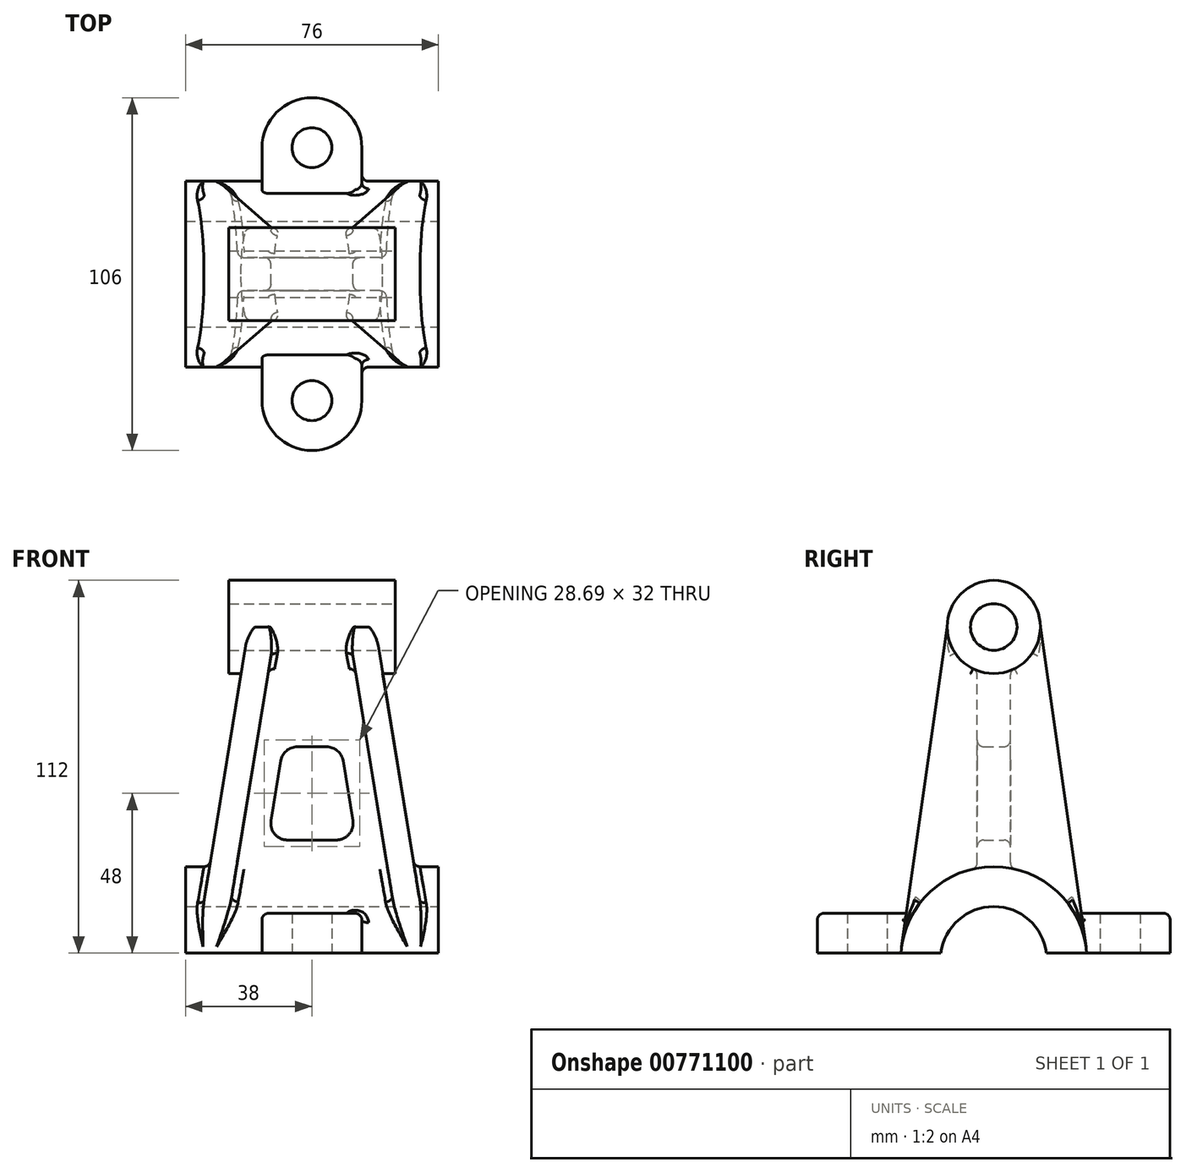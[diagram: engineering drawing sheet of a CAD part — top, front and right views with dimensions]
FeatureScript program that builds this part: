
annotation { "Feature Type Name" : "Feature", "Feature Type Description" : "" }
export const myFeature = defineFeature(function(context is Context, id is Id, definition is map)
    precondition{}
    {
        {
            var Q0;
            Q0=qCreatedBy(makeId("Right.planeOp"),FACE);
            var sketch = newSketch(context, id + "F0", { "sketchPlane" : qUnion([Q0])});
            skArc(sketch, "E0", {"start": v(27.93, 2) * mm, "mid": v(0, 28) * mm, "end": v(-27.93, 2) * mm});
            skArc(sketch, "E1", {"start": v(15.87, 2) * mm, "mid": v(0, 16) * mm, "end": v(-15.87, 2) * mm});
            skLineSegment(sketch, "E2", {"start": v(0, 0) * mm, "end": v(36.01, 0) * mm, "construction": true});
            skLineSegment(sketch, "E3", {"start": v(-27.93, 2) * mm, "end": v(27.93, 2) * mm});
            skSolve(sketch);
        }
        {
            var Q0;
            Q0=qSketchRegion(id+"F0",true);
            extrude(context, id + "F1", {"entities" : qUnion([Q0]), "depth" : 76 * mm, "offsetDistance" : 25 * mm, "symmetric" : true});
        }
        {
            var Q0;
            Q0=qCreatedBy(makeId("Right.planeOp"),FACE);
            var sketch = newSketch(context, id + "F2", { "sketchPlane" : qUnion([Q0])});
            skLineSegment(sketch, "E4", {"start": v(0, 0) * mm, "end": v(0, 100) * mm, "construction": true});
            skCircle(sketch, "E5", {"center": v(0, 100) * mm, "radius": 7 * mm});
            skCircle(sketch, "E6", {"center": v(0, 100) * mm, "radius": 14 * mm});
            skSolve(sketch);
        }
        {
            var Q0;
            Q0=qSketchRegion(id+"F2",true);
            var Q1;
            Q1=makeQuery(id+"F2.imprint","IMPRINT",FACE,{"disambiguationData":[TD([[makeQuery(id+"F2.imprint","IMPRINT",EDGE,{"derivedFrom":sQuery(id+"F2.wireOp",EDGE,"E5")}),1.0]])]});
            extrude(context, id + "F3", {"entities" : qUnion([Q0, Q1]), "depth" : 50 * mm, "offsetDistance" : 25 * mm, "symmetric" : true});
        }
        {
            var Q0;
            Q0=qCreatedBy(makeId("Front.planeOp"),FACE);
            var sketch = newSketch(context, id + "F4", { "sketchPlane" : qUnion([Q0])});
            skLineSegment(sketch, "E7", {"start": v(0, 0) * mm, "end": v(0, 29.66) * mm, "construction": true});
            skLineSegment(sketch, "E8", {"start": v(-19, 100) * mm, "end": v(19, 100) * mm});
            skLineSegment(sketch, "E9.0", {"start": v(35, 2) * mm, "end": v(-35, 2) * mm});
            skLineSegment(sketch, "E10", {"start": v(19, 100) * mm, "end": v(35, 2) * mm});
            skLineSegment(sketch, "E11.MirrorCS", {"start": v(-19, 100) * mm, "end": v(-35, 2) * mm});
            skLineSegment(sketch, "E12", {"start": v(-30.76, 28) * mm, "end": v(30.76, 28) * mm});
            skLineSegment(sketch, "E13.0", {"start": v(9.35, 59.8) * mm, "end": v(12.29, 41.8) * mm});
            skLineSegment(sketch, "E14.MirrorCS", {"start": v(-9.35, 59.8) * mm, "end": v(-12.29, 41.8) * mm});
            skLineSegment(sketch, "E15.trimOffspring", {"start": v(-4.42, 64) * mm, "end": v(4.42, 64) * mm});
            skLineSegment(sketch, "E16.trimOffspring", {"start": v(-7.35, 36) * mm, "end": v(7.35, 36) * mm});
            skPoint(sketch, "E17.orphan", {"position": v(-38, 2) * mm});
            skPoint(sketch, "E18.orphan", {"position": v(38, 2) * mm});
            skLineSegment(sketch, "E19", {"start": v(10.9, 100) * mm, "end": v(26.9, 2) * mm});
            skLineSegment(sketch, "E20.MirrorCS", {"start": v(-10.9, 100) * mm, "end": v(-26.9, 2) * mm});
            skPoint(sketch, "E21.visualSharp", {"position": v(-8.67, 64) * mm});
            skArc(sketch, "E21.filletArc", {"start": v(-4.42, 64) * mm, "mid": v(-7.65, 62.8) * mm, "end": v(-9.35, 59.8) * mm});
            skPoint(sketch, "E22.visualSharp", {"position": v(8.67, 64) * mm});
            skArc(sketch, "E22.filletArc", {"start": v(9.35, 59.8) * mm, "mid": v(7.65, 62.8) * mm, "end": v(4.42, 64) * mm});
            skPoint(sketch, "E23.visualSharp", {"position": v(-13.24, 36) * mm});
            skArc(sketch, "E23.filletArc", {"start": v(-12.29, 41.8) * mm, "mid": v(-11.16, 37.76) * mm, "end": v(-7.35, 36) * mm});
            skPoint(sketch, "E24.visualSharp", {"position": v(13.24, 36) * mm});
            skArc(sketch, "E24.filletArc", {"start": v(7.35, 36) * mm, "mid": v(11.16, 37.76) * mm, "end": v(12.29, 41.8) * mm});
            skSolve(sketch);
        }
        {
            var Q0;
            Q0=qSketchRegion(id+"F4",true);
            extrude(context, id + "F5", {"entities" : qUnion([Q0]), "operationType" : NewBodyOperationType.ADD, "depth" : 10 * mm, "offsetDistance" : 25 * mm, "symmetric" : true});
        }
        {
            var Q0;
            {var subQ0=sQuery(id+"F4.wireOp",EDGE,"E10");var subQ1=sQuery(id+"F4.wireOp",EDGE,"E8");var subQ2=makeQuery(id+"F4.imprint","INTERSECT",VERTEX,{"derivedFrom":[subQ1,subQ0]});Q0=makeQuery(id+"F4.imprint","IMPRINT",FACE,{"disambiguationData":[TD([[makeQuery(id+"F4.imprint","IMPRINT",EDGE,{"disambiguationData":[TD([[subQ2,1.0]])],"derivedFrom":subQ1}),-1.0]])]});}
            var Q1;
            {var subQ0=sQuery(id+"F4.wireOp",EDGE,"E11.MirrorCS");var subQ1=sQuery(id+"F4.wireOp",EDGE,"E8");var subQ2=makeQuery(id+"F4.imprint","INTERSECT",VERTEX,{"derivedFrom":[subQ1,subQ0]});Q1=makeQuery(id+"F4.imprint","IMPRINT",FACE,{"disambiguationData":[TD([[makeQuery(id+"F4.imprint","IMPRINT",EDGE,{"disambiguationData":[TD([[subQ2,-1.0]])],"derivedFrom":subQ1}),-1.0]])]});}
            var Q2;
            {var subQ0=sQuery(id+"F4.wireOp",EDGE,"E11.MirrorCS");var subQ1=sQuery(id+"F4.wireOp",EDGE,"E9.0");var subQ2=makeQuery(id+"F4.imprint","INTERSECT",VERTEX,{"derivedFrom":[subQ1,subQ0]});Q2=makeQuery(id+"F4.imprint","IMPRINT",FACE,{"disambiguationData":[TD([[makeQuery(id+"F4.imprint","IMPRINT",EDGE,{"disambiguationData":[TD([[subQ2,1.0]])],"derivedFrom":subQ1}),-1.0]])]});}
            var Q3;
            {var subQ0=sQuery(id+"F4.wireOp",EDGE,"E10");var subQ1=sQuery(id+"F4.wireOp",EDGE,"E9.0");var subQ2=makeQuery(id+"F4.imprint","INTERSECT",VERTEX,{"derivedFrom":[subQ1,subQ0]});Q3=makeQuery(id+"F4.imprint","IMPRINT",FACE,{"disambiguationData":[TD([[makeQuery(id+"F4.imprint","IMPRINT",EDGE,{"disambiguationData":[TD([[subQ2,-1.0]])],"derivedFrom":subQ1}),-1.0]])]});}
            var Q4;
            {var subQ0=sQuery(id+"F0.wireOp",EDGE,"E3");var subQ1=sQuery(id+"F0.wireOp",EDGE,"E0");Q4=makeQuery(id+"F1.opExtrude","CAP_VERTEX",VERTEX,{"disambiguationData":[OSD([subQ1,subQ0]),TDD([makeQuery(id+"F0.imprint","INTERSECT",VERTEX,{"disambiguationData":[OD(1.0)],"derivedFrom":[subQ1,subQ0]})])],"isStart":false});}
            extrude(context, id + "F6", {"entities" : qUnion([Q0, Q1, Q2, Q3]), "operationType" : NewBodyOperationType.ADD, "endBound" : BoundingType.UP_TO_VERTEX, "depth" : 25 * mm, "endBoundEntityVertex" : qUnion([Q4]), "offsetDistance" : 25 * mm});
        }
        {
            var Q0;
            Q0=qCreatedBy(makeId("Right.planeOp"),FACE);
            var sketch = newSketch(context, id + "F7", { "sketchPlane" : qUnion([Q0])});
            skCircle(sketch, "E25.0", {"center": v(0, 100) * mm, "radius": 14 * mm});
            skArc(sketch, "E26.0", {"start": v(27.93, 2) * mm, "mid": v(0, 28) * mm, "end": v(-27.93, 2) * mm});
            skLineSegment(sketch, "E27.0", {"start": v(-27.93, 100) * mm, "end": v(-14, 100) * mm});
            skLineSegment(sketch, "E28", {"start": v(-14, 100) * mm, "end": v(-27.72, 3.96) * mm});
            skLineSegment(sketch, "E29.0", {"start": v(-27.93, 100) * mm, "end": v(-27.93, 2) * mm});
            skSolve(sketch);
        }
        {
            var Q0;
            Q0=makeQuery(id+"F7.imprint","IMPRINT",FACE,{"disambiguationData":[TD([[makeQuery(id+"F7.imprint","IMPRINT",EDGE,{"derivedFrom":sQuery(id+"F7.wireOp",EDGE,"E27.0")}),-1.0]])]});
            extrude(context, id + "F8", {"entities" : qUnion([Q0]), "operationType" : NewBodyOperationType.REMOVE, "oppositeDirection" : true, "depth" : 76 * mm, "offsetDistance" : 25 * mm, "symmetric" : true});
        }
        {
            var Q0;
            Q0=qCreatedBy(makeId("Right.planeOp"),FACE);
            var sketch = newSketch(context, id + "F9", { "sketchPlane" : qUnion([Q0])});
            skLineSegment(sketch, "E30.bottom", {"start": v(0, 0) * mm, "end": v(47.87, 0) * mm});
            skLineSegment(sketch, "E30.top", {"start": v(0, 124.66) * mm, "end": v(47.87, 124.66) * mm});
            skLineSegment(sketch, "E30.left", {"start": v(0, 0) * mm, "end": v(0, 124.66) * mm});
            skLineSegment(sketch, "E30.right", {"start": v(47.87, 0) * mm, "end": v(47.87, 124.66) * mm});
            skSolve(sketch);
        }
        {
            var Q0;
            Q0=qSketchRegion(id+"F9",true);
            extrude(context, id + "F10", {"entities" : qUnion([Q0]), "operationType" : NewBodyOperationType.REMOVE, "oppositeDirection" : true, "depth" : 76 * mm, "offsetDistance" : 25 * mm, "symmetric" : true});
        }
        {
            var Q0;
            Q0=makeQuery(id+"F1.opExtrude","SWEPT_BODY",BODY,{"disambiguationData":[OSD([sQuery(id+"F0.wireOp",EDGE,"E0"),sQuery(id+"F0.wireOp",EDGE,"E3")])]});
            var Q1;
            Q1=qCreatedBy(makeId("Front.planeOp"),FACE);
            mirror(context, id + "F11", {"operationType" : NewBodyOperationType.ADD, "entities" : qUnion([Q0]), "mirrorPlane" : qUnion([Q1])});
        }
        {
            var Q0;
            Q0=makeQuery(id+"F1.opExtrude","SWEPT_FACE",FACE,{"disambiguationData":[OSD([sQuery(id+"F0.wireOp",EDGE,"E3")])]});
            var sketch = newSketch(context, id + "F12", { "sketchPlane" : qUnion([Q0])});
            skLineSegment(sketch, "E31", {"start": v(0, 38) * mm, "end": v(0, -38) * mm, "construction": true});
            skLineSegment(sketch, "E32", {"start": v(0, 0) * mm, "end": v(9.46, 0) * mm, "construction": true});
            skArc(sketch, "E33.0.startCap", {"start": v(-15, 38) * mm, "mid": v(0, 53) * mm, "end": v(15, 38) * mm});
            skArc(sketch, "E33.0.endCap", {"start": v(15, -38) * mm, "mid": v(0, -53) * mm, "end": v(-15, -38) * mm});
            skLineSegment(sketch, "E33.0.left", {"start": v(15, 38) * mm, "end": v(15, -38) * mm});
            skLineSegment(sketch, "E33.0.right", {"start": v(-15, 38) * mm, "end": v(-15, -38) * mm});
            skCircle(sketch, "E34", {"center": v(0, 38) * mm, "radius": 6 * mm});
            skCircle(sketch, "E35", {"center": v(0, -38) * mm, "radius": 6 * mm});
            skSolve(sketch);
        }
        {
            var Q0;
            Q0=qSketchRegion(id+"F12",true);
            extrude(context, id + "F13", {"entities" : qUnion([Q0]), "operationType" : NewBodyOperationType.ADD, "oppositeDirection" : true, "depth" : 12 * mm, "offsetDistance" : 25 * mm});
        }
        {
            var Q0;
            {var subQ0=sQuery(id+"F0.wireOp",EDGE,"E1");Q0=makeQuery(id+"F0.imprint","IMPRINT",FACE,{"disambiguationData":[TD([[makeQuery(id+"F0.imprint","IMPRINT",EDGE,{"derivedFrom":subQ0}),1.0]])]});}
            extrude(context, id + "F14", {"entities" : qUnion([Q0]), "operationType" : NewBodyOperationType.REMOVE, "oppositeDirection" : true, "depth" : 76 * mm, "offsetDistance" : 25 * mm, "symmetric" : true});
        }
        {
            var Q0;
            Q0=makeQuery(id+"F2.imprint","IMPRINT",FACE,{"disambiguationData":[TD([[makeQuery(id+"F2.imprint","IMPRINT",EDGE,{"derivedFrom":sQuery(id+"F2.wireOp",EDGE,"E5")}),1.0]])]});
            extrude(context, id + "F15", {"entities" : qUnion([Q0]), "operationType" : NewBodyOperationType.REMOVE, "oppositeDirection" : true, "depth" : 50 * mm, "offsetDistance" : 25 * mm, "symmetric" : true});
        }
        {
            var Q0;
            {var subQ0=sQuery(id+"F12.wireOp",EDGE,"E33.0.startCap");var subQ2=sQuery(id+"F12.wireOp",EDGE,"E33.0.left");Q0=makeQuery(id+"F13.boolean.opBoolean","SPLIT",EDGE,{"disambiguationData":[TD([makeQuery(id+"F13.opExtrude","SWEPT_FACE",FACE,{"disambiguationData":[OSD([subQ0])]})])],"derivedFrom":makeQuery(id+"F13.opExtrude","CAP_EDGE",EDGE,{"disambiguationData":[OSD([subQ2])],"isStart":false})});}
            var Q1;
            {var subQ5=sQuery(id+"F4.wireOp",EDGE,"E10");var subQ13=sQuery(id+"F0.wireOp",EDGE,"E0");var subQ14=makeQuery(id+"F1.opExtrude","SWEPT_FACE",FACE,{"disambiguationData":[OSD([subQ13])]});var subQ15=makeQuery(id+"F8.boolean.opBoolean","MERGE",FACE,{"derivedFrom":[makeQuery(id+"F6.boolean.opBoolean","SPLIT",FACE,{"disambiguationData":[TD([makeQuery(id+"F5.opExtrude","SWEPT_FACE",FACE,{"disambiguationData":[OSD([subQ5])]})])],"derivedFrom":subQ14}),makeQuery(id+"F6.boolean.opBoolean","SPLIT",FACE,{"disambiguationData":[TD([makeQuery(id+"F6.opExtrude","SWEPT_FACE",FACE,{"disambiguationData":[OSD([sQuery(id+"F4.wireOp",EDGE,"E19")])]})])],"derivedFrom":subQ14}),makeQuery(id+"F8.opExtrude","SWEPT_FACE",FACE,{"disambiguationData":[OSD([sQuery(id+"F7.wireOp",EDGE,"E26.0")])]})]});Q1=makeQuery(id+"F13.boolean.opBoolean","INTERSECT",EDGE,{"disambiguationData":[OD(0.0)],"derivedFrom":[makeQuery(id+"F11.boolean.opBoolean","MERGE",FACE,{"derivedFrom":[subQ15,makeQuery(id+"F11.opPattern","COPY",FACE,{"derivedFrom":subQ15,"instanceName":"1"})]}),makeQuery(id+"F13.opExtrude","SWEPT_FACE",FACE,{"disambiguationData":[OSD([sQuery(id+"F12.wireOp",EDGE,"E33.0.left")])]})]});}
            var Q2;
            {var subQ0=sQuery(id+"F4.wireOp",EDGE,"E10");Q2=makeQuery(id+"F8.boolean.opBoolean","INTERSECT",EDGE,{"derivedFrom":[makeQuery(id+"F6.boolean.opBoolean","MERGE",FACE,{"derivedFrom":[makeQuery(id+"F5.opExtrude","SWEPT_FACE",FACE,{"disambiguationData":[OSD([subQ0])]}),makeQuery(id+"F6.opExtrude","SWEPT_FACE",FACE,{"disambiguationData":[OSD([subQ0])]})]}),makeQuery(id+"F8.opExtrude","SWEPT_FACE",FACE,{"disambiguationData":[OSD([sQuery(id+"F7.wireOp",EDGE,"E28")])]})]});}
            var Q3;
            Q3=makeQuery(id+"F8.boolean.opBoolean","INTERSECT",EDGE,{"derivedFrom":[makeQuery(id+"F6.opExtrude","SWEPT_FACE",FACE,{"disambiguationData":[OSD([sQuery(id+"F4.wireOp",EDGE,"E19")])]}),makeQuery(id+"F8.opExtrude","SWEPT_FACE",FACE,{"disambiguationData":[OSD([sQuery(id+"F7.wireOp",EDGE,"E28")])]})]});
            var Q4;
            {var subQ0=sQuery(id+"F4.wireOp",EDGE,"E11.MirrorCS");Q4=makeQuery(id+"F8.boolean.opBoolean","INTERSECT",EDGE,{"derivedFrom":[makeQuery(id+"F6.boolean.opBoolean","MERGE",FACE,{"derivedFrom":[makeQuery(id+"F5.opExtrude","SWEPT_FACE",FACE,{"disambiguationData":[OSD([subQ0])]}),makeQuery(id+"F6.opExtrude","SWEPT_FACE",FACE,{"disambiguationData":[OSD([subQ0])]})]}),makeQuery(id+"F8.opExtrude","SWEPT_FACE",FACE,{"disambiguationData":[OSD([sQuery(id+"F7.wireOp",EDGE,"E28")])]})]});}
            var Q5;
            Q5=makeQuery(id+"F8.boolean.opBoolean","INTERSECT",EDGE,{"derivedFrom":[makeQuery(id+"F6.opExtrude","SWEPT_FACE",FACE,{"disambiguationData":[OSD([sQuery(id+"F4.wireOp",EDGE,"E20.MirrorCS")])]}),makeQuery(id+"F8.opExtrude","SWEPT_FACE",FACE,{"disambiguationData":[OSD([sQuery(id+"F7.wireOp",EDGE,"E28")])]})]});
            var Q6;
            Q6=makeQuery(id+"F6.boolean.opBoolean","INTERSECT",EDGE,{"derivedFrom":[makeQuery(id+"F3.opExtrude","SWEPT_FACE",FACE,{"disambiguationData":[OSD([sQuery(id+"F2.wireOp",EDGE,"E6")])]}),makeQuery(id+"F6.opExtrude","SWEPT_FACE",FACE,{"disambiguationData":[OSD([sQuery(id+"F4.wireOp",EDGE,"E20.MirrorCS")])]})]});
            var Q7;
            Q7=makeQuery(id+"F6.boolean.opBoolean","INTERSECT",EDGE,{"derivedFrom":[makeQuery(id+"F1.opExtrude","SWEPT_FACE",FACE,{"disambiguationData":[OSD([sQuery(id+"F0.wireOp",EDGE,"E0")])]}),makeQuery(id+"F6.opExtrude","SWEPT_FACE",FACE,{"disambiguationData":[OSD([sQuery(id+"F4.wireOp",EDGE,"E20.MirrorCS")])]})]});
            var Q8;
            Q8=makeQuery(id+"F6.boolean.opBoolean","INTERSECT",EDGE,{"derivedFrom":[makeQuery(id+"F1.opExtrude","SWEPT_FACE",FACE,{"disambiguationData":[OSD([sQuery(id+"F0.wireOp",EDGE,"E0")])]}),makeQuery(id+"F6.opExtrude","SWEPT_FACE",FACE,{"disambiguationData":[OSD([sQuery(id+"F4.wireOp",EDGE,"E19")])]})]});
            var Q9;
            Q9=makeQuery(id+"F6.boolean.opBoolean","INTERSECT",EDGE,{"derivedFrom":[makeQuery(id+"F3.opExtrude","SWEPT_FACE",FACE,{"disambiguationData":[OSD([sQuery(id+"F2.wireOp",EDGE,"E6")])]}),makeQuery(id+"F6.opExtrude","SWEPT_FACE",FACE,{"disambiguationData":[OSD([sQuery(id+"F4.wireOp",EDGE,"E19")])]})]});
            var Q10;
            Q10=makeQuery(id+"F6.boolean.opBoolean","INTERSECT",EDGE,{"derivedFrom":[makeQuery(id+"F5.opExtrude","CAP_FACE",FACE,{"disambiguationData":[OSD([sQuery(id+"F4.wireOp",EDGE,"E8"),sQuery(id+"F4.wireOp",EDGE,"E9.0"),sQuery(id+"F4.wireOp",EDGE,"E10"),sQuery(id+"F4.wireOp",EDGE,"E11.MirrorCS"),sQuery(id+"F4.wireOp",EDGE,"E13.0"),sQuery(id+"F4.wireOp",EDGE,"E14.MirrorCS"),sQuery(id+"F4.wireOp",EDGE,"E15.trimOffspring"),sQuery(id+"F4.wireOp",EDGE,"E16.trimOffspring")])],"isStart":false}),makeQuery(id+"F6.opExtrude","SWEPT_FACE",FACE,{"disambiguationData":[OSD([sQuery(id+"F4.wireOp",EDGE,"E20.MirrorCS")])]})]});
            var Q11;
            Q11=makeQuery(id+"F5.boolean.opBoolean","INTERSECT",EDGE,{"derivedFrom":[makeQuery(id+"F1.opExtrude","SWEPT_FACE",FACE,{"disambiguationData":[OSD([sQuery(id+"F0.wireOp",EDGE,"E0")])]}),makeQuery(id+"F5.opExtrude","CAP_FACE",FACE,{"disambiguationData":[OSD([sQuery(id+"F4.wireOp",EDGE,"E8"),sQuery(id+"F4.wireOp",EDGE,"E9.0"),sQuery(id+"F4.wireOp",EDGE,"E10"),sQuery(id+"F4.wireOp",EDGE,"E11.MirrorCS"),sQuery(id+"F4.wireOp",EDGE,"E13.0"),sQuery(id+"F4.wireOp",EDGE,"E14.MirrorCS"),sQuery(id+"F4.wireOp",EDGE,"E15.trimOffspring"),sQuery(id+"F4.wireOp",EDGE,"E16.trimOffspring")])],"isStart":false})]});
            var Q12;
            Q12=makeQuery(id+"F6.boolean.opBoolean","INTERSECT",EDGE,{"derivedFrom":[makeQuery(id+"F5.opExtrude","CAP_FACE",FACE,{"disambiguationData":[OSD([sQuery(id+"F4.wireOp",EDGE,"E8"),sQuery(id+"F4.wireOp",EDGE,"E9.0"),sQuery(id+"F4.wireOp",EDGE,"E10"),sQuery(id+"F4.wireOp",EDGE,"E11.MirrorCS"),sQuery(id+"F4.wireOp",EDGE,"E13.0"),sQuery(id+"F4.wireOp",EDGE,"E14.MirrorCS"),sQuery(id+"F4.wireOp",EDGE,"E15.trimOffspring"),sQuery(id+"F4.wireOp",EDGE,"E16.trimOffspring")])],"isStart":false}),makeQuery(id+"F6.opExtrude","SWEPT_FACE",FACE,{"disambiguationData":[OSD([sQuery(id+"F4.wireOp",EDGE,"E19")])]})]});
            var Q13;
            Q13=makeQuery(id+"F5.boolean.opBoolean","INTERSECT",EDGE,{"derivedFrom":[makeQuery(id+"F3.opExtrude","SWEPT_FACE",FACE,{"disambiguationData":[OSD([sQuery(id+"F2.wireOp",EDGE,"E6")])]}),makeQuery(id+"F5.opExtrude","CAP_FACE",FACE,{"disambiguationData":[OSD([sQuery(id+"F4.wireOp",EDGE,"E8"),sQuery(id+"F4.wireOp",EDGE,"E9.0"),sQuery(id+"F4.wireOp",EDGE,"E10"),sQuery(id+"F4.wireOp",EDGE,"E11.MirrorCS"),sQuery(id+"F4.wireOp",EDGE,"E13.0"),sQuery(id+"F4.wireOp",EDGE,"E14.MirrorCS"),sQuery(id+"F4.wireOp",EDGE,"E15.trimOffspring"),sQuery(id+"F4.wireOp",EDGE,"E16.trimOffspring")])],"isStart":false})]});
            var Q14;
            Q14=makeQuery(id+"F5.opExtrude","CAP_EDGE",EDGE,{"disambiguationData":[OSD([sQuery(id+"F4.wireOp",EDGE,"E15.trimOffspring")])],"isStart":false});
            var Q15;
            Q15=makeQuery(id+"F5.opExtrude","CAP_EDGE",EDGE,{"disambiguationData":[OSD([sQuery(id+"F4.wireOp",EDGE,"E14.MirrorCS")])],"isStart":false});
            var Q16;
            Q16=makeQuery(id+"F5.opExtrude","CAP_EDGE",EDGE,{"disambiguationData":[OSD([sQuery(id+"F4.wireOp",EDGE,"E16.trimOffspring")])],"isStart":false});
            var Q17;
            Q17=makeQuery(id+"F5.opExtrude","CAP_EDGE",EDGE,{"disambiguationData":[OSD([sQuery(id+"F4.wireOp",EDGE,"E13.0")])],"isStart":false});
            fillet(context, id + "F16", {"entities" : qUnion([Q0, Q1, Q2, Q3, Q4, Q5, Q6, Q7, Q8, Q9, Q10, Q11, Q12, Q13, Q14, Q15, Q16, Q17]), "radius" : 2 * mm, "tangentPropagation" : true, "allowEdgeOverflow" : false});
        }
        {
            var Q0;
            Q0=qCreatedBy(makeId("Right.planeOp"),FACE);
            var sketch = newSketch(context, id + "F17", { "sketchPlane" : qUnion([Q0])});
            skLineSegment(sketch, "E36.bottom", {"start": v(0, 0) * mm, "end": v(75.65, 0) * mm});
            skLineSegment(sketch, "E36.top", {"start": v(0, 124.31) * mm, "end": v(75.65, 124.31) * mm});
            skLineSegment(sketch, "E36.left", {"start": v(0, 0) * mm, "end": v(0, 124.31) * mm});
            skLineSegment(sketch, "E36.right", {"start": v(75.65, 0) * mm, "end": v(75.65, 124.31) * mm});
            skSolve(sketch);
        }
        {
            var Q0;
            Q0=makeQuery(id+"F17.imprint","IMPRINT",FACE,{"disambiguationData":[TD([[makeQuery(id+"F17.imprint","IMPRINT",EDGE,{"derivedFrom":sQuery(id+"F17.wireOp",EDGE,"E36.bottom")}),1.0]])]});
            extrude(context, id + "F18", {"entities" : qUnion([Q0]), "operationType" : NewBodyOperationType.REMOVE, "oppositeDirection" : true, "depth" : 76 * mm, "offsetDistance" : 25 * mm, "symmetric" : true});
        }
        {
            var Q0;
            Q0=makeQuery(id+"F1.opExtrude","SWEPT_BODY",BODY,{"disambiguationData":[OSD([sQuery(id+"F0.wireOp",EDGE,"E0"),sQuery(id+"F0.wireOp",EDGE,"E3")])]});
            var Q1;
            Q1=qCreatedBy(makeId("Front.planeOp"),FACE);
            mirror(context, id + "F19", {"operationType" : NewBodyOperationType.ADD, "entities" : qUnion([Q0]), "mirrorPlane" : qUnion([Q1])});
        }
        {
            var Q0;
            {var subQ0=makeQuery(id+"F6.boolean.opBoolean","INTERSECT",EDGE,{"derivedFrom":[makeQuery(id+"F1.opExtrude","SWEPT_FACE",FACE,{"disambiguationData":[OSD([sQuery(id+"F0.wireOp",EDGE,"E0")])]}),makeQuery(id+"F6.opExtrude","SWEPT_FACE",FACE,{"disambiguationData":[OSD([sQuery(id+"F4.wireOp",EDGE,"E10")])]})]});var subQ1=makeQuery(id+"F11.boolean.opBoolean","MERGE",EDGE,{"derivedFrom":[subQ0,makeQuery(id+"F11.opPattern","COPY",EDGE,{"derivedFrom":subQ0,"instanceName":"1"})]});Q0=makeQuery(id+"F19.boolean.opBoolean","MERGE",EDGE,{"derivedFrom":[subQ1,makeQuery(id+"F19.opPattern","COPY",EDGE,{"derivedFrom":subQ1,"instanceName":"1"})]});}
            var Q1;
            {var subQ0=makeQuery(id+"F6.boolean.opBoolean","INTERSECT",EDGE,{"derivedFrom":[makeQuery(id+"F1.opExtrude","SWEPT_FACE",FACE,{"disambiguationData":[OSD([sQuery(id+"F0.wireOp",EDGE,"E0")])]}),makeQuery(id+"F6.opExtrude","SWEPT_FACE",FACE,{"disambiguationData":[OSD([sQuery(id+"F4.wireOp",EDGE,"E11.MirrorCS")])]})]});var subQ1=makeQuery(id+"F11.boolean.opBoolean","MERGE",EDGE,{"derivedFrom":[subQ0,makeQuery(id+"F11.opPattern","COPY",EDGE,{"derivedFrom":subQ0,"instanceName":"1"})]});Q1=makeQuery(id+"F19.boolean.opBoolean","MERGE",EDGE,{"derivedFrom":[subQ1,makeQuery(id+"F19.opPattern","COPY",EDGE,{"derivedFrom":subQ1,"instanceName":"1"})]});}
            var Q2;
            {var subQ0=makeQuery(id+"F5.opExtrude","SWEPT_EDGE",EDGE,{"disambiguationData":[OSD([sQuery(id+"F4.wireOp",EDGE,"E13.0"),sQuery(id+"F4.wireOp",EDGE,"E15.trimOffspring")])]});var subQ1=makeQuery(id+"F11.boolean.opBoolean","MERGE",EDGE,{"derivedFrom":[subQ0,makeQuery(id+"F11.opPattern","COPY",EDGE,{"derivedFrom":subQ0,"instanceName":"1"})]});Q2=makeQuery(id+"F19.boolean.opBoolean","MERGE",EDGE,{"derivedFrom":[subQ1,makeQuery(id+"F19.opPattern","COPY",EDGE,{"derivedFrom":subQ1,"instanceName":"1"})]});}
            var Q3;
            {var subQ0=makeQuery(id+"F5.opExtrude","SWEPT_EDGE",EDGE,{"disambiguationData":[OSD([sQuery(id+"F4.wireOp",EDGE,"E13.0"),sQuery(id+"F4.wireOp",EDGE,"E16.trimOffspring")])]});var subQ1=makeQuery(id+"F11.boolean.opBoolean","MERGE",EDGE,{"derivedFrom":[subQ0,makeQuery(id+"F11.opPattern","COPY",EDGE,{"derivedFrom":subQ0,"instanceName":"1"})]});Q3=makeQuery(id+"F19.boolean.opBoolean","MERGE",EDGE,{"derivedFrom":[subQ1,makeQuery(id+"F19.opPattern","COPY",EDGE,{"derivedFrom":subQ1,"instanceName":"1"})]});}
            var Q4;
            {var subQ0=makeQuery(id+"F5.opExtrude","SWEPT_EDGE",EDGE,{"disambiguationData":[OSD([sQuery(id+"F4.wireOp",EDGE,"E14.MirrorCS"),sQuery(id+"F4.wireOp",EDGE,"E16.trimOffspring")])]});var subQ1=makeQuery(id+"F11.boolean.opBoolean","MERGE",EDGE,{"derivedFrom":[subQ0,makeQuery(id+"F11.opPattern","COPY",EDGE,{"derivedFrom":subQ0,"instanceName":"1"})]});Q4=makeQuery(id+"F19.boolean.opBoolean","MERGE",EDGE,{"derivedFrom":[subQ1,makeQuery(id+"F19.opPattern","COPY",EDGE,{"derivedFrom":subQ1,"instanceName":"1"})]});}
            var Q5;
            {var subQ0=makeQuery(id+"F5.opExtrude","SWEPT_EDGE",EDGE,{"disambiguationData":[OSD([sQuery(id+"F4.wireOp",EDGE,"E14.MirrorCS"),sQuery(id+"F4.wireOp",EDGE,"E15.trimOffspring")])]});var subQ1=makeQuery(id+"F11.boolean.opBoolean","MERGE",EDGE,{"derivedFrom":[subQ0,makeQuery(id+"F11.opPattern","COPY",EDGE,{"derivedFrom":subQ0,"instanceName":"1"})]});Q5=makeQuery(id+"F19.boolean.opBoolean","MERGE",EDGE,{"derivedFrom":[subQ1,makeQuery(id+"F19.opPattern","COPY",EDGE,{"derivedFrom":subQ1,"instanceName":"1"})]});}
            fillet(context, id + "F20", {"entities" : qUnion([Q0, Q1, Q2, Q3, Q4, Q5]), "radius" : 2 * mm, "tangentPropagation" : true, "allowEdgeOverflow" : false});
        }
    });
